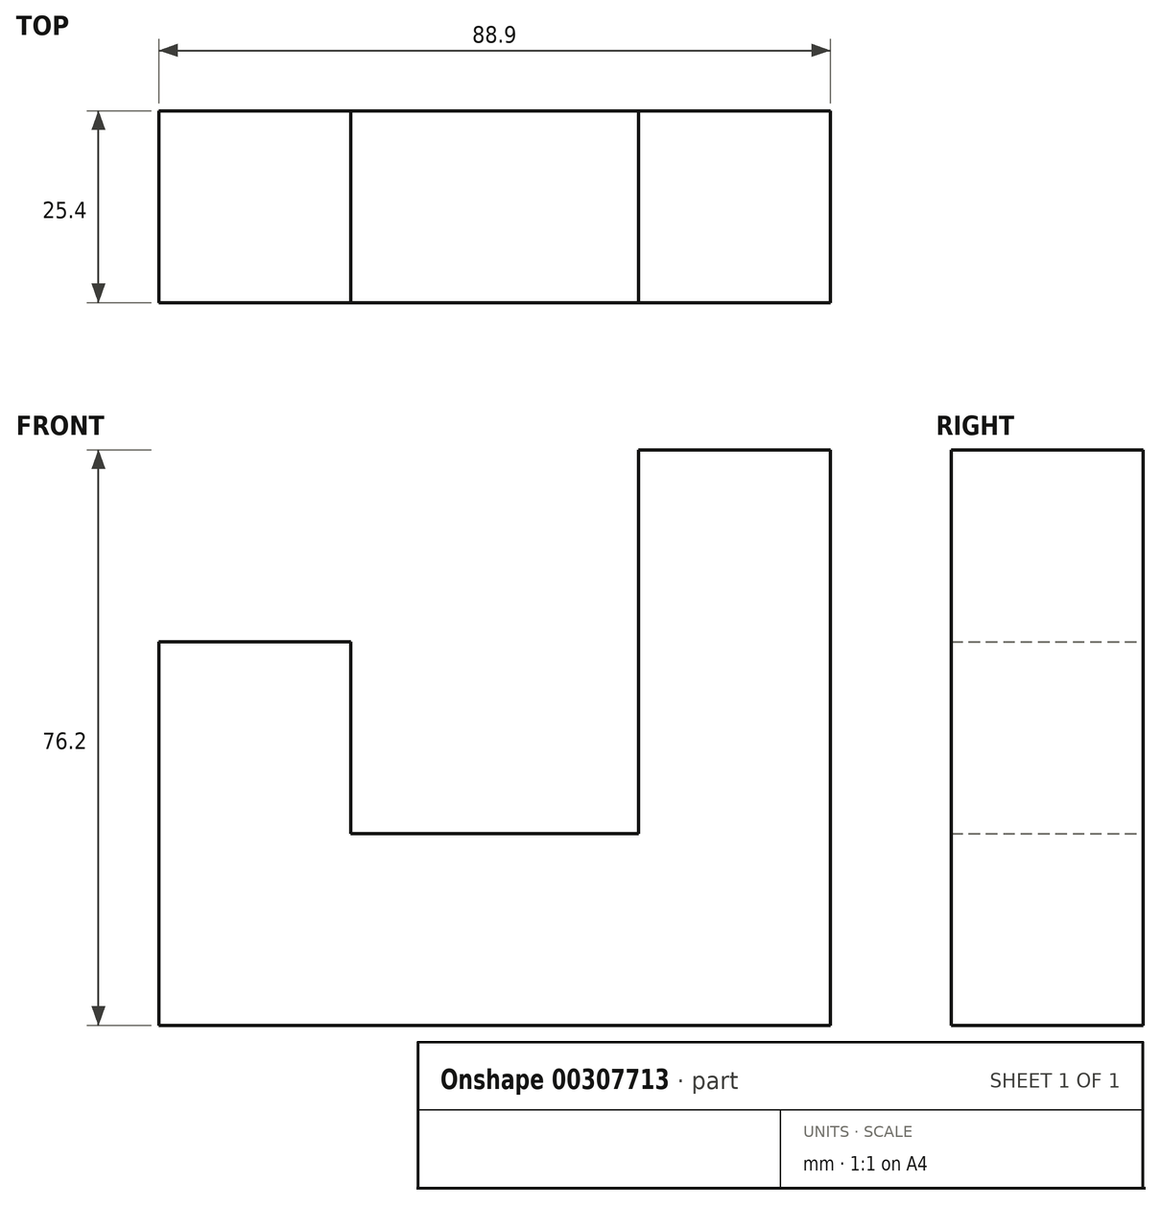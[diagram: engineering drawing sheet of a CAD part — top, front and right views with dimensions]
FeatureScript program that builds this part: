
annotation { "Feature Type Name" : "Feature", "Feature Type Description" : "" }
export const myFeature = defineFeature(function(context is Context, id is Id, definition is map)
    precondition{}
    {
        {
            var Q0;
            Q0=qCreatedBy(makeId("Front.planeOp"),FACE);
            var sketch = newSketch(context, id + "F0", { "sketchPlane" : qUnion([Q0])});
            skLineSegment(sketch, "E0", {"start": v(-40.7, -25.4) * mm, "end": v(48.2, -25.4) * mm});
            skLineSegment(sketch, "E1", {"start": v(48.2, -25.4) * mm, "end": v(48.2, 50.8) * mm});
            skLineSegment(sketch, "E2", {"start": v(48.2, 50.8) * mm, "end": v(22.8, 50.8) * mm});
            skLineSegment(sketch, "E3", {"start": v(22.8, 50.8) * mm, "end": v(22.8, 0) * mm});
            skLineSegment(sketch, "E4", {"start": v(22.8, 0) * mm, "end": v(-15.3, 0) * mm});
            skLineSegment(sketch, "E5", {"start": v(-15.3, 0) * mm, "end": v(-15.3, 25.4) * mm});
            skLineSegment(sketch, "E6", {"start": v(-15.3, 25.4) * mm, "end": v(-40.7, 25.4) * mm});
            skLineSegment(sketch, "E7", {"start": v(-40.7, 25.4) * mm, "end": v(-40.7, -25.4) * mm});
            skSolve(sketch);
        }
        {
            var Q0;
            Q0=makeQuery(id+"F0.imprint","IMPRINT",FACE,{"disambiguationData":[TD([[makeQuery(id+"F0.imprint","IMPRINT",EDGE,{"derivedFrom":sQuery(id+"F0.wireOp",EDGE,"E0")}),1.0]])]});
            extrude(context, id + "F1", {"entities" : qUnion([Q0]), "depth" : 25.4 * mm});
        }
    });
